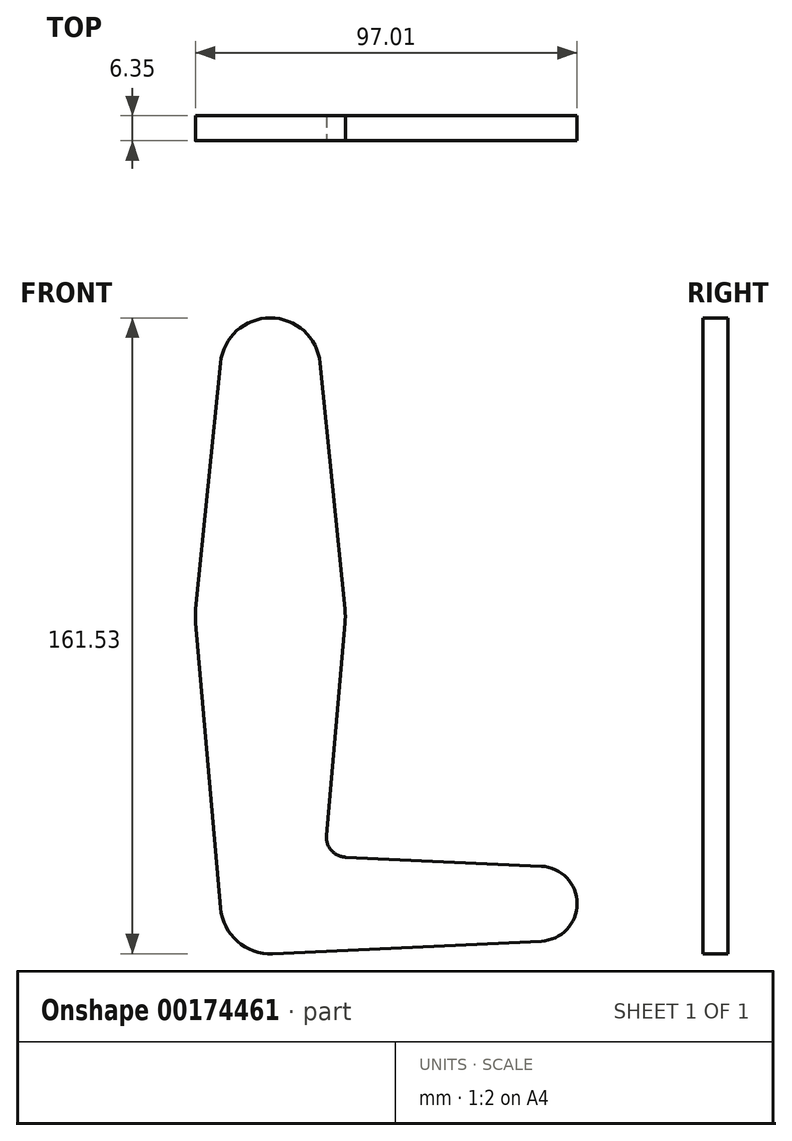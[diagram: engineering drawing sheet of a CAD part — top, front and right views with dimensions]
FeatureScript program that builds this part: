
annotation { "Feature Type Name" : "Feature", "Feature Type Description" : "" }
export const myFeature = defineFeature(function(context is Context, id is Id, definition is map)
    precondition{}
    {
        {
            var Q0;
            Q0=qCreatedBy(makeId("Front.planeOp"),FACE);
            var sketch = newSketch(context, id + "F0", { "sketchPlane" : qUnion([Q0])});
            skCircle(sketch, "E0", {"center": v(0, 0) * mm, "radius": 19.05 * mm});
            skCircle(sketch, "E1", {"center": v(0, 63.16) * mm, "radius": 12.7 * mm});
            skCircle(sketch, "E2", {"center": v(0, -72.97) * mm, "radius": 12.7 * mm});
            skCircle(sketch, "E3", {"center": v(68.43, -72.97) * mm, "radius": 9.53 * mm});
            skLineSegment(sketch, "E4", {"start": v(0, 63.16) * mm, "end": v(0, 0) * mm, "construction": true});
            skLineSegment(sketch, "E5", {"start": v(0, -72.97) * mm, "end": v(68.43, -72.97) * mm, "construction": true});
            skLineSegment(sketch, "E6", {"start": v(0, 0) * mm, "end": v(0, -72.97) * mm, "construction": true});
            skLineSegment(sketch, "E7", {"start": v(-12.64, 64.44) * mm, "end": v(-18.95, 1.92) * mm});
            skLineSegment(sketch, "E8", {"start": v(-18.98, -1.66) * mm, "end": v(-12.65, -74.08) * mm});
            skLineSegment(sketch, "E9", {"start": v(12.64, 64.44) * mm, "end": v(18.95, 1.92) * mm});
            skLineSegment(sketch, "E10", {"start": v(18.98, -1.66) * mm, "end": v(12.65, -74.08) * mm});
            skLineSegment(sketch, "E11", {"start": v(0.59, -60.29) * mm, "end": v(68.88, -63.46) * mm});
            skLineSegment(sketch, "E12", {"start": v(0.59, -85.66) * mm, "end": v(68.88, -82.49) * mm});
            skSolve(sketch);
        }
        {
            var Q0;
            Q0 = qSketchRegion(id + "F0", true);
            extrude(context, id + "F1", {"entities" : qUnion([Q0]), "depth" : 6.35 * mm});
        }
        {
            var Q0;
            Q0=makeQuery(id+"F1.opExtrude","SWEPT_EDGE",EDGE,{"disambiguationData":[OSD([sQuery(id+"F0.wireOp",EDGE,"E10"),sQuery(id+"F0.wireOp",EDGE,"E11")])]});
            fillet(context, id + "F2", {"entities" : qUnion([Q0]), "radius" : 5.08 * mm, "tangentPropagation" : true, "allowEdgeOverflow" : false});
        }
    });
